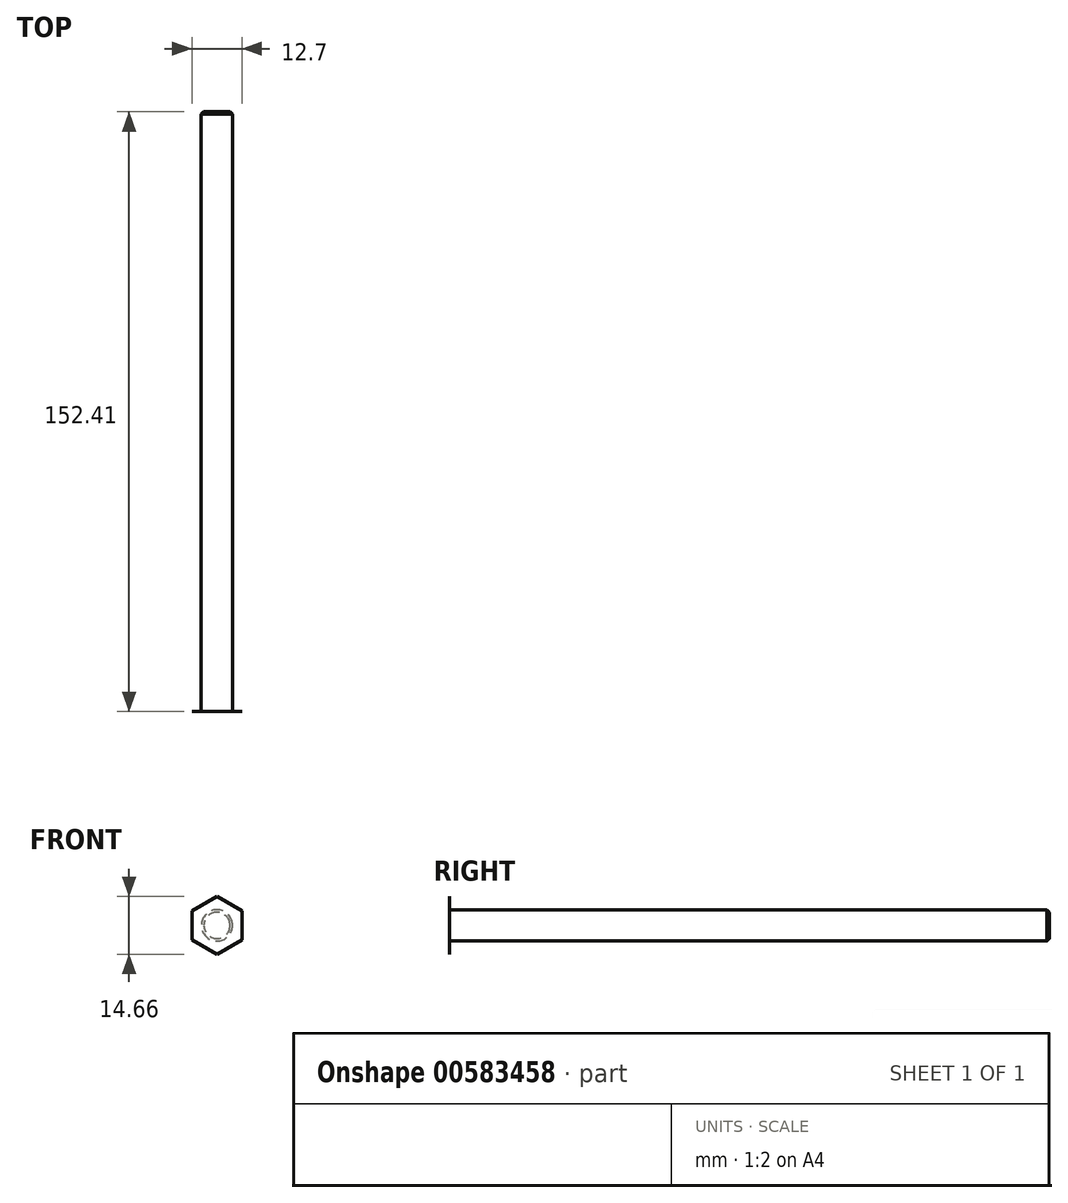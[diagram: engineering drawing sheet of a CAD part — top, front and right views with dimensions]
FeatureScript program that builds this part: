
annotation { "Feature Type Name" : "Feature", "Feature Type Description" : "" }
export const myFeature = defineFeature(function(context is Context, id is Id, definition is map)
    precondition{}
    {
        {
            assignVariable(context, id + "F0", {"name" : "BoltLen", "anyValue" : 152.4 * mm});
        }
        {
            assignVariable(context, id + "F1", {"name" : "HeadDepth", "anyValue" : 7 / 812.8 * mm});
        }
        {
            var Q0;
            Q0=qCreatedBy(makeId("Front.planeOp"),FACE);
            var sketch = newSketch(context, id + "F2", { "sketchPlane" : qUnion([Q0])});
            skCircle(sketch, "E0", {"center": v(0, 0) * mm, "radius": 3.97 * mm});
            skSolve(sketch);
        }
        {
            var Q0;
            Q0=qSketchRegion(id+"F2",true);
            extrude(context, id + "F3", {"entities" : qUnion([Q0]), "oppositeDirection" : true, "depth" : getVariable(context, 'BoltLen'), "offsetDistance" : 25.4 * mm});
        }
        {
            var Q0;
            Q0=qCreatedBy(makeId("Front.planeOp"),FACE);
            var sketch = newSketch(context, id + "F4", { "sketchPlane" : qUnion([Q0])});
            skCircle(sketch, "E1.cCircle", {"center": v(0, 0) * mm, "radius": 6.35 * mm, "construction": true});
            skLineSegment(sketch, "E1.0", {"start": v(6.35, -3.67) * mm, "end": v(0, -7.33) * mm});
            skLineSegment(sketch, "E1.1", {"start": v(0, -7.33) * mm, "end": v(-6.35, -3.67) * mm});
            skLineSegment(sketch, "E1.2", {"start": v(-6.35, -3.67) * mm, "end": v(-6.35, 3.67) * mm});
            skLineSegment(sketch, "E1.3", {"start": v(-6.35, 3.67) * mm, "end": v(0, 7.33) * mm});
            skLineSegment(sketch, "E1.4", {"start": v(0, 7.33) * mm, "end": v(6.35, 3.67) * mm});
            skLineSegment(sketch, "E1.5", {"start": v(6.35, 3.67) * mm, "end": v(6.35, -3.67) * mm});
            skPoint(sketch, "E1.0.midPoint", {"position": v(3.18, -5.5) * mm});
            skSolve(sketch);
        }
        {
            var Q0;
            Q0=qSketchRegion(id+"F4",true);
            extrude(context, id + "F5", {"entities" : qUnion([Q0]), "operationType" : NewBodyOperationType.ADD, "depth" : getVariable(context, 'HeadDepth'), "offsetDistance" : 25.4 * mm});
        }
        {
            var Q0;
            Q0=makeQuery(id+"F3.opExtrude","CAP_EDGE",EDGE,{"disambiguationData":[OSD([sQuery(id+"F2.wireOp",EDGE,"E0")])],"isStart":false});
            chamfer(context, id + "F6", {"entities" : qUnion([Q0]), "width" : 0.64 * mm, "tangentPropagation" : true});
        }
        {
            var Q0;
            Q0=qCreatedBy(makeId("Top.planeOp"),FACE);
            var sketch = newSketch(context, id + "F7", { "sketchPlane" : qUnion([Q0])});
            skLineSegment(sketch, "E2", {"start": v(13.43, -1.47) * mm, "end": v(13.43, -5.56) * mm});
            skLineSegment(sketch, "E3", {"start": v(13.43, -5.56) * mm, "end": v(6.35, -5.56) * mm});
            skLineSegment(sketch, "E4", {"start": v(6.35, -5.56) * mm, "end": v(13.43, -1.47) * mm});
            skLineSegment(sketch, "E5", {"start": v(0, 0) * mm, "end": v(0, -5.56) * mm, "construction": true});
            skSolve(sketch);
        }
        {
            var Q0;
            Q0=qSketchRegion(id+"F7",true);
            var Q1;
            Q1=sQuery(id+"F7.wireOp",EDGE,"E5");
            revolve(context, id + "F8", {"operationType" : NewBodyOperationType.REMOVE, "entities" : qUnion([Q0]), "axis" : qUnion([Q1]), "revolveType" : RevolveType.FULL, "oppositeDirection" : true});
        }
    });
